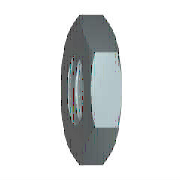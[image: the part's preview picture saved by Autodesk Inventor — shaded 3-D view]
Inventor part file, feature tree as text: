
AUTODESK INVENTOR PART (.ipt)
format: ipt  version: 2015 (Build 190159000, 159)  size: 162,816 bytes
history: native  units: mm (DEFAULTED — no unit token found)
features: sketch x3, other x2, extrude x1, hole x1, plane x1
ambient origin geometry x7: Origin, YZ Plane, XZ Plane, X Axis, Y Axis, Z Axis, Center Point
bodies: Body1 (feature_tree)
feature tree (8):
  extrude  "Bryła"  Depth=11.547005mm
  other  "Faza1"
  hole  "Gwint"  [1 undecoded]
  other  "Work Axis1"
  plane  "Work Plane1"
  sketch  "Szkic1"
  sketch  "Szkic2"
  sketch  "Szkic3"
note: 1 required parameter value undecoded (feature->parameter linkage not recoverable at this tier; creation-order binding heuristic only, values carry confidence <= 0.55)
